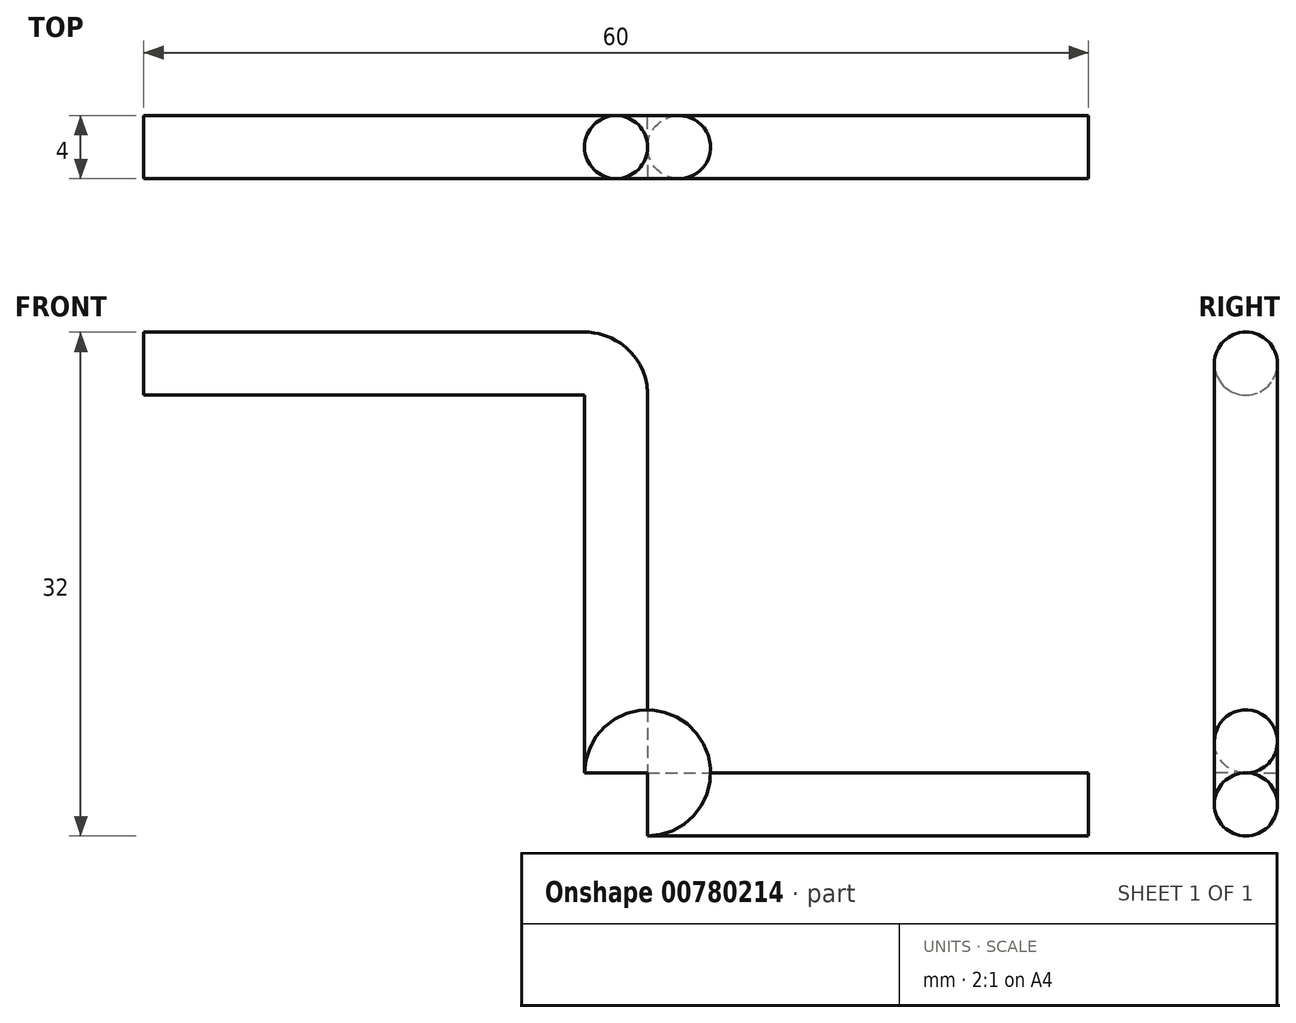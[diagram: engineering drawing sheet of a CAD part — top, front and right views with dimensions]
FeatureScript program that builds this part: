
annotation { "Feature Type Name" : "Feature", "Feature Type Description" : "" }
export const myFeature = defineFeature(function(context is Context, id is Id, definition is map)
    precondition{}
    {
        {
            var Q0;
            Q0=qCreatedBy(makeId("Front.planeOp"),FACE);
            var sketch = newSketch(context, id + "F0", { "sketchPlane" : qUnion([Q0])});
            skLineSegment(sketch, "E0", {"start": v(0, 0) * mm, "end": v(0, -23) * mm});
            skLineSegment(sketch, "E1", {"start": v(2, -25) * mm, "end": v(30, -25) * mm});
            skPoint(sketch, "E2.visualSharp", {"position": v(0, -25) * mm});
            skArc(sketch, "E2.filletArc", {"start": v(0, -23) * mm, "mid": v(0.59, -24.41) * mm, "end": v(2, -25) * mm});
            skLineSegment(sketch, "E3", {"start": v(0, 0) * mm, "end": v(0, 1) * mm});
            skLineSegment(sketch, "E4", {"start": v(-2, 3) * mm, "end": v(-30, 3) * mm});
            skPoint(sketch, "E5.visualSharp", {"position": v(0, 3) * mm});
            skArc(sketch, "E5.filletArc", {"start": v(0, 1) * mm, "mid": v(-0.59, 2.41) * mm, "end": v(-2, 3) * mm});
            skSolve(sketch);
        }
        {
            var Q0;
            Q0=qCreatedBy(makeId("Right.planeOp"),FACE);
            cPlane(context, id + "F1", {"entities" : qUnion([Q0]), "cplaneType" : CPlaneType.OFFSET, "offset" : 30 * mm, "oppositeDirection" : true, "width" : 150 * mm, "height" : 150 * mm});
        }
        {
            var Q0;
            Q0=qCreatedBy(id+"F1.planeOp",FACE);
            var sketch = newSketch(context, id + "F2", { "sketchPlane" : qUnion([Q0])});
            skCircle(sketch, "E6", {"center": v(0, 3) * mm, "radius": 2 * mm});
            skSolve(sketch);
        }
        {
            var Q0;
            Q0=makeQuery(id+"F2.imprint","IMPRINT",FACE,{"disambiguationData":[TD([[makeQuery(id+"F2.imprint","IMPRINT",EDGE,{"derivedFrom":sQuery(id+"F2.wireOp",EDGE,"E6")}),1.0]])]});
            var Q1;
            Q1=sQuery(id+"F0.wireOp",EDGE,"E4");
            var Q2;
            Q2=sQuery(id+"F0.wireOp",EDGE,"E5.filletArc");
            var Q3;
            Q3=sQuery(id+"F0.wireOp",EDGE,"E0");
            var Q4;
            Q4=sQuery(id+"F0.wireOp",EDGE,"E3");
            var Q5;
            Q5=sQuery(id+"F0.wireOp",EDGE,"E2.filletArc");
            var Q6;
            Q6=sQuery(id+"F0.wireOp",EDGE,"E1");
            sweep(context, id + "F3", {"profiles" : qUnion([Q0]), "path" : qUnion([Q1, Q2, Q3, Q4, Q5, Q6])});
        }
    });
